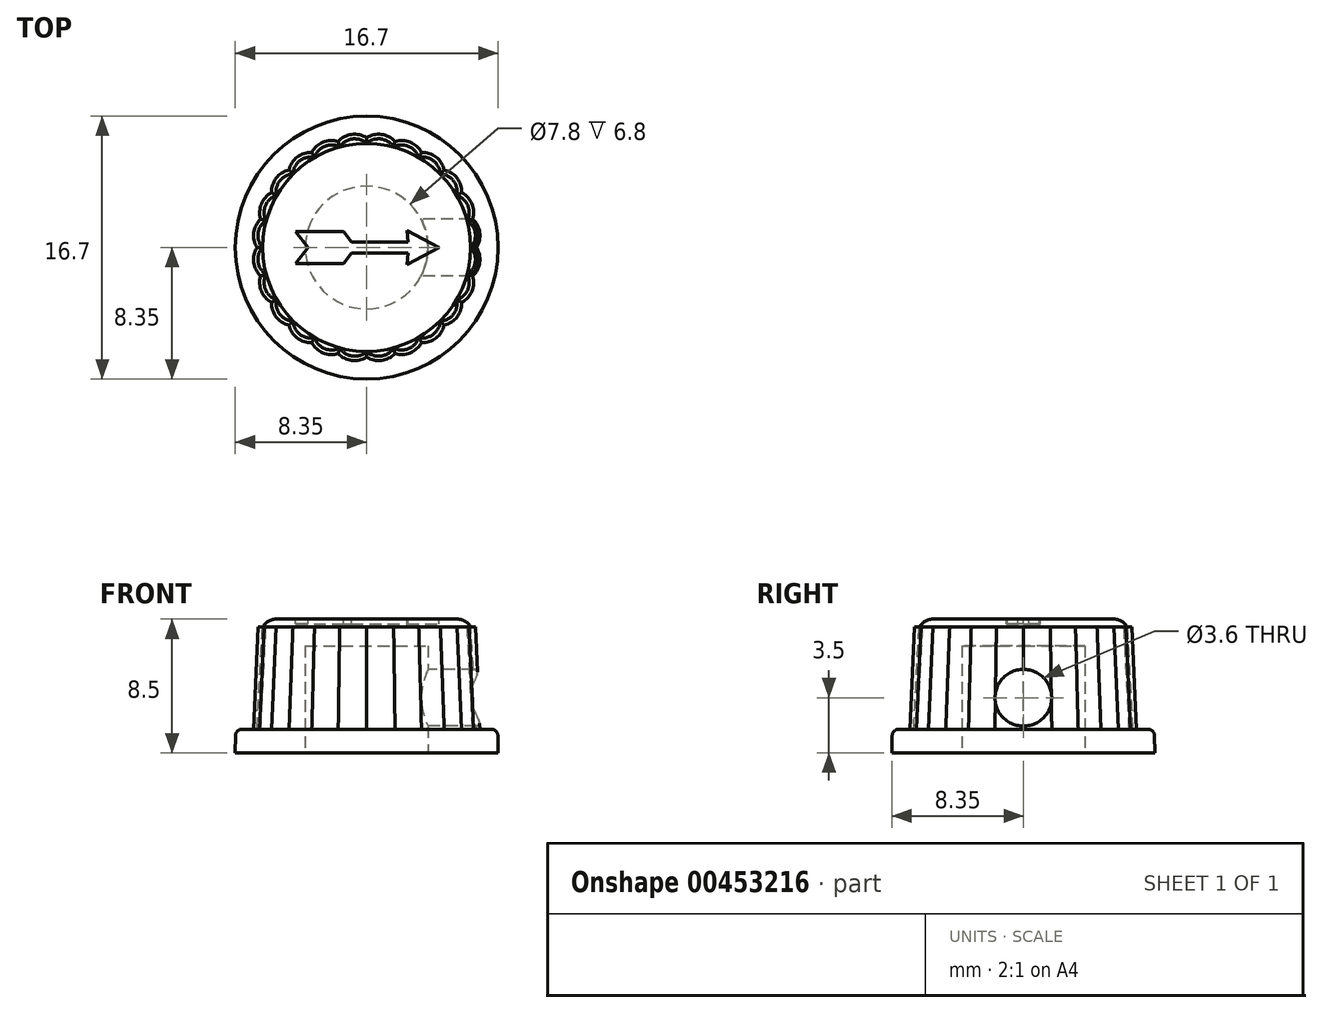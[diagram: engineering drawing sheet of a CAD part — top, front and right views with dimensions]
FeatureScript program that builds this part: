
annotation { "Feature Type Name" : "Feature", "Feature Type Description" : "" }
export const myFeature = defineFeature(function(context is Context, id is Id, definition is map)
    precondition{}
    {
        {
            var Q0;
            Q0=qCreatedBy(makeId("Top.planeOp"),FACE);
            var sketch = newSketch(context, id + "F0", { "sketchPlane" : qUnion([Q0])});
            skCircle(sketch, "E0", {"center": v(0, 0) * mm, "radius": 8.35 * mm});
            skSolve(sketch);
        }
        {
            var Q0;
            Q0 = qSketchRegion(id + "F0", true);
            extrude(context, id + "F1", {"entities" : qUnion([Q0]), "depth" : 1.5 * mm, "hasDraft" : true, "draftAngle" : 1 * degree, "draftPullDirection" : true});
        }
        {
            var Q0;
            Q0=makeQuery(id+"F1.opExtrude","CAP_FACE",FACE,{"disambiguationData":[OSD([sQuery(id+"F0.wireOp",EDGE,"E0")])],"isStart":false});
            var sketch = newSketch(context, id + "F2", { "sketchPlane" : qUnion([Q0])});
            skCircle(sketch, "E1", {"center": v(0, 0) * mm, "radius": 6.9 * mm});
            skSolve(sketch);
        }
        {
            var Q0;
            Q0 = qSketchRegion(id + "F2", true);
            extrude(context, id + "F3", {"entities" : qUnion([Q0]), "operationType" : NewBodyOperationType.ADD, "depth" : 6.5 * mm, "hasDraft" : true, "draftAngle" : 2.5 * degree, "draftPullDirection" : true});
        }
        {
            var Q0;
            Q0=makeQuery(id+"F3.opExtrude","CAP_FACE",FACE,{"disambiguationData":[OSD([sQuery(id+"F2.wireOp",EDGE,"E1")])],"isStart":false});
            var sketch = newSketch(context, id + "F4", { "sketchPlane" : qUnion([Q0])});
            skCircle(sketch, "E2", {"center": v(0, 0) * mm, "radius": 6.6 * mm});
            skSolve(sketch);
        }
        {
            var Q0;
            Q0 = qSketchRegion(id + "F4", true);
            extrude(context, id + "F5", {"entities" : qUnion([Q0]), "operationType" : NewBodyOperationType.ADD, "depth" : .5 * mm});
        }
        {
            var Q0;
            Q0=makeQuery(id+"F3.opExtrude","CAP_FACE",FACE,{"disambiguationData":[OSD([sQuery(id+"F2.wireOp",EDGE,"E1")])],"isStart":false});
            var sketch = newSketch(context, id + "F6", { "sketchPlane" : qUnion([Q0])});
            skLineSegment(sketch, "E3", {"start": v(0, 0) * mm, "end": v(17.23, 0) * mm, "construction": true});
            skLineSegment(sketch, "E4", {"start": v(0, 0) * mm, "end": v(18.83, 5.05) * mm, "construction": true});
            skArc(sketch, "E5", {"start": v(6.62, 0) * mm, "mid": v(6.9, 0.9) * mm, "end": v(6.4, 1.71) * mm});
            skArc(sketch, "E6.1.0", {"start": v(6.4, -1.71) * mm, "mid": v(6.9, -0.9) * mm, "end": v(6.62, 0) * mm});
            skArc(sketch, "E6.2.0", {"start": v(5.73, -3.3) * mm, "mid": v(6.43, -2.66) * mm, "end": v(6.4, -1.71) * mm});
            skArc(sketch, "E6.3.0", {"start": v(4.68, -4.68) * mm, "mid": v(5.52, -4.23) * mm, "end": v(5.73, -3.3) * mm});
            skArc(sketch, "E6.4.0", {"start": v(3.3, -5.73) * mm, "mid": v(4.23, -5.52) * mm, "end": v(4.68, -4.68) * mm});
            skArc(sketch, "E6.5.0", {"start": v(1.71, -6.4) * mm, "mid": v(2.66, -6.43) * mm, "end": v(3.3, -5.73) * mm});
            skArc(sketch, "E6.6.0", {"start": v(0, -6.62) * mm, "mid": v(0.9, -6.9) * mm, "end": v(1.71, -6.4) * mm});
            skArc(sketch, "E6.7.0", {"start": v(-1.71, -6.4) * mm, "mid": v(-0.9, -6.9) * mm, "end": v(0, -6.62) * mm});
            skArc(sketch, "E6.8.0", {"start": v(-3.3, -5.73) * mm, "mid": v(-2.66, -6.43) * mm, "end": v(-1.71, -6.4) * mm});
            skArc(sketch, "E6.9.0", {"start": v(-4.68, -4.68) * mm, "mid": v(-4.23, -5.52) * mm, "end": v(-3.3, -5.73) * mm});
            skArc(sketch, "E6.10.0", {"start": v(-5.73, -3.3) * mm, "mid": v(-5.52, -4.23) * mm, "end": v(-4.68, -4.68) * mm});
            skArc(sketch, "E6.11.0", {"start": v(-6.4, -1.71) * mm, "mid": v(-6.43, -2.66) * mm, "end": v(-5.73, -3.3) * mm});
            skArc(sketch, "E6.12.0", {"start": v(-6.62, 0) * mm, "mid": v(-6.9, -0.9) * mm, "end": v(-6.4, -1.71) * mm});
            skArc(sketch, "E6.13.0", {"start": v(-6.4, 1.71) * mm, "mid": v(-6.9, 0.9) * mm, "end": v(-6.62, 0) * mm});
            skArc(sketch, "E6.14.0", {"start": v(-5.73, 3.3) * mm, "mid": v(-6.43, 2.66) * mm, "end": v(-6.4, 1.71) * mm});
            skArc(sketch, "E6.15.0", {"start": v(-4.68, 4.68) * mm, "mid": v(-5.52, 4.23) * mm, "end": v(-5.73, 3.3) * mm});
            skArc(sketch, "E6.16.0", {"start": v(-3.3, 5.73) * mm, "mid": v(-4.23, 5.52) * mm, "end": v(-4.68, 4.68) * mm});
            skArc(sketch, "E6.17.0", {"start": v(-1.71, 6.4) * mm, "mid": v(-2.66, 6.43) * mm, "end": v(-3.3, 5.73) * mm});
            skArc(sketch, "E6.18.0", {"start": v(0, 6.62) * mm, "mid": v(-0.9, 6.9) * mm, "end": v(-1.71, 6.4) * mm});
            skArc(sketch, "E6.19.0", {"start": v(1.71, 6.4) * mm, "mid": v(0.9, 6.9) * mm, "end": v(0, 6.62) * mm});
            skArc(sketch, "E6.20.0", {"start": v(3.3, 5.73) * mm, "mid": v(2.66, 6.43) * mm, "end": v(1.71, 6.4) * mm});
            skArc(sketch, "E6.21.0", {"start": v(4.68, 4.68) * mm, "mid": v(4.23, 5.52) * mm, "end": v(3.3, 5.73) * mm});
            skArc(sketch, "E6.22.0", {"start": v(5.73, 3.3) * mm, "mid": v(5.52, 4.23) * mm, "end": v(4.68, 4.68) * mm});
            skArc(sketch, "E6.23.0", {"start": v(6.4, 1.71) * mm, "mid": v(6.43, 2.66) * mm, "end": v(5.73, 3.3) * mm});
            skPoint(sketch, "E6.center", {"position": v(0, 0) * mm});
            skLineSegment(sketch, "E6.anchor1", {"start": v(0, 0) * mm, "end": v(6.62, 0) * mm, "construction": true});
            skLineSegment(sketch, "E6.anchor2", {"start": v(0, 0) * mm, "end": v(6.4, 1.71) * mm, "construction": true});
            skSolve(sketch);
        }
        {
            var Q0;
            Q0 = qSketchRegion(id + "F6", true);
            var Q1;
            Q1=makeQuery(id+"F1.opExtrude","CAP_FACE",FACE,{"disambiguationData":[OSD([sQuery(id+"F0.wireOp",EDGE,"E0")])],"isStart":false});
            extrude(context, id + "F7", {"entities" : qUnion([Q0]), "operationType" : NewBodyOperationType.ADD, "endBound" : BoundingType.UP_TO_SURFACE, "oppositeDirection" : true, "endBoundEntityFace" : qUnion([Q1]), "depth" : 25 * mm, "hasDraft" : true, "draftAngle" : 2.5 * degree});
        }
        {
            var Q0;
            Q0=makeQuery(id+"F5.opExtrude","CAP_EDGE",EDGE,{"disambiguationData":[OSD([sQuery(id+"F4.wireOp",EDGE,"E2")])],"isStart":false});
            fillet(context, id + "F8", {"entities" : qUnion([Q0]), "radius" : 1 * mm, "tangentPropagation" : true, "allowEdgeOverflow" : false});
        }
        {
            var Q0;
            Q0=makeQuery(id+"F1.opExtrude","CAP_EDGE",EDGE,{"disambiguationData":[OSD([sQuery(id+"F0.wireOp",EDGE,"E0")])],"isStart":false});
            fillet(context, id + "F9", {"entities" : qUnion([Q0]), "radius" : .4 * mm, "tangentPropagation" : true, "allowEdgeOverflow" : false});
        }
        {
            var Q0;
            Q0=makeQuery(id+"F1.opExtrude","CAP_FACE",FACE,{"disambiguationData":[OSD([sQuery(id+"F0.wireOp",EDGE,"E0")])],"isStart":true});
            var sketch = newSketch(context, id + "F10", { "sketchPlane" : qUnion([Q0])});
            skCircle(sketch, "E7", {"center": v(0, 0) * mm, "radius": 3.9 * mm});
            skSolve(sketch);
        }
        {
            var Q0;
            Q0 = qSketchRegion(id + "F10", true);
            extrude(context, id + "F11", {"entities" : qUnion([Q0]), "operationType" : NewBodyOperationType.REMOVE, "oppositeDirection" : true, "offsetDistance" : 25 * mm, "depth" : 6.8 * mm});
        }
        {
            var Q0;
            Q0=qCreatedBy(makeId("Right.planeOp"),FACE);
            var sketch = newSketch(context, id + "F12", { "sketchPlane" : qUnion([Q0])});
            skCircle(sketch, "E8", {"center": v(0, 3.5) * mm, "radius": 1.8 * mm});
            skSolve(sketch);
        }
        {
            var Q0;
            Q0 = qSketchRegion(id + "F12", true);
            extrude(context, id + "F13", {"entities" : qUnion([Q0]), "operationType" : NewBodyOperationType.REMOVE, "depth" : 25 * mm});
        }
        {
            var Q0;
            Q0=makeQuery(id+"F5.opExtrude","CAP_FACE",FACE,{"disambiguationData":[OSD([sQuery(id+"F4.wireOp",EDGE,"E2")])],"isStart":false});
            var sketch = newSketch(context, id + "F14", { "sketchPlane" : qUnion([Q0])});
            skLineSegment(sketch, "E9", {"start": v(-3.73, 0) * mm, "end": v(-4.5, 1.02) * mm});
            skLineSegment(sketch, "E10", {"start": v(-4.5, 1.02) * mm, "end": v(-1.47, 1.02) * mm});
            skLineSegment(sketch, "E11", {"start": v(-1.47, 1.02) * mm, "end": v(-0.96, 0.35) * mm});
            skLineSegment(sketch, "E12", {"start": v(-0.96, 0.35) * mm, "end": v(2.64, 0.35) * mm});
            skLineSegment(sketch, "E13", {"start": v(2.64, 0.35) * mm, "end": v(2.57, 1.07) * mm});
            skLineSegment(sketch, "E14", {"start": v(2.57, 1.07) * mm, "end": v(4.6, 0) * mm});
            skLineSegment(sketch, "E15", {"start": v(-3.86, 0) * mm, "end": v(5.2, 0) * mm, "construction": true});
            skLineSegment(sketch, "E16.MirrorCS", {"start": v(2.64, -0.35) * mm, "end": v(2.57, -1.07) * mm});
            skLineSegment(sketch, "E17.MirrorCS", {"start": v(-0.96, -0.35) * mm, "end": v(2.64, -0.35) * mm});
            skLineSegment(sketch, "E18.MirrorCS", {"start": v(-1.47, -1.02) * mm, "end": v(-0.96, -0.35) * mm});
            skLineSegment(sketch, "E19.MirrorCS", {"start": v(-4.5, -1.02) * mm, "end": v(-1.47, -1.02) * mm});
            skLineSegment(sketch, "E20.MirrorCS", {"start": v(-3.73, 0) * mm, "end": v(-4.5, -1.02) * mm});
            skLineSegment(sketch, "E21.MirrorCS", {"start": v(2.57, -1.07) * mm, "end": v(4.6, 0) * mm});
            skSolve(sketch);
        }
        {
            var Q0;
            Q0 = qSketchRegion(id + "F14", true);
            extrude(context, id + "F15", {"entities" : qUnion([Q0]), "operationType" : NewBodyOperationType.REMOVE, "oppositeDirection" : true, "depth" : .3 * mm});
        }
    });
